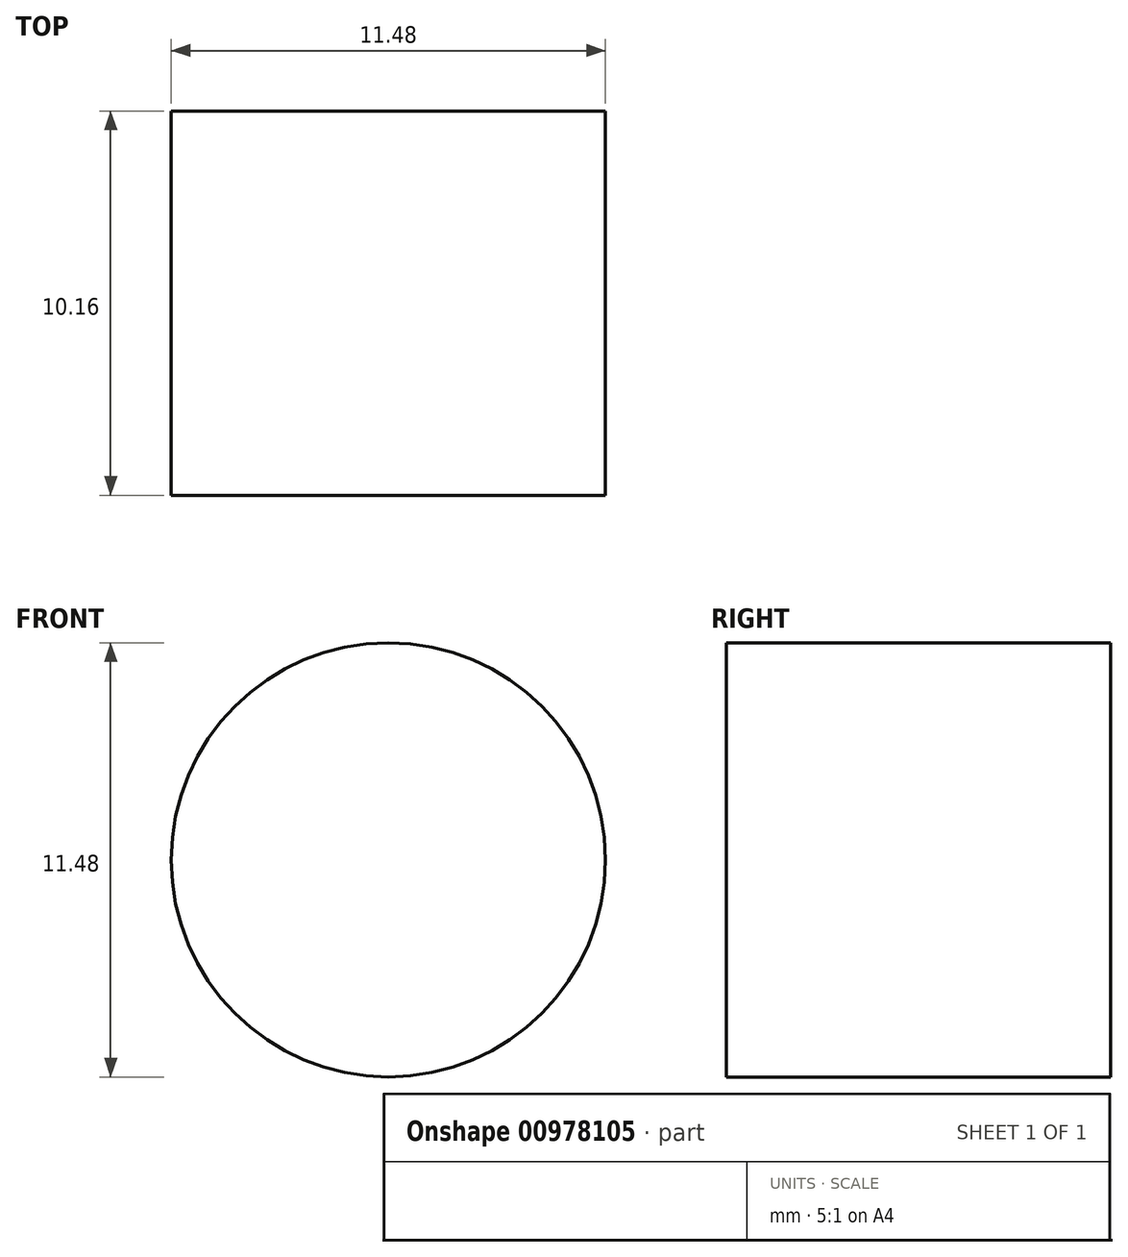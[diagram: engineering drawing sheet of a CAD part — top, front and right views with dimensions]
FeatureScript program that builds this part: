
annotation { "Feature Type Name" : "Feature", "Feature Type Description" : "" }
export const myFeature = defineFeature(function(context is Context, id is Id, definition is map)
    precondition{}
    {
        {
            var Q0;
            Q0=qCreatedBy(makeId("Front.planeOp"),FACE);
            var sketch = newSketch(context, id + "F0", { "sketchPlane" : qUnion([Q0])});
            skCircle(sketch, "E0", {"center": v(0, 0) * mm, "radius": 5.74 * mm});
            skSolve(sketch);
        }
        {
            var Q0;
            Q0=makeQuery(id+"F0.imprint","IMPRINT",FACE,{"disambiguationData":[TD([[makeQuery(id+"F0.imprint","IMPRINT",EDGE,{"derivedFrom":sQuery(id+"F0.wireOp",EDGE,"E0")}),1.0]])]});
            var Q1;
            Q1=sQuery(id+"F0.wireOp",EDGE,"E0");
            extrude(context, id + "F1", {"entities" : qUnion([Q0]), "surfaceEntities" : qUnion([Q1]), "depth" : 10.16 * mm, "offsetDistance" : 25.4 * mm});
        }
    });
